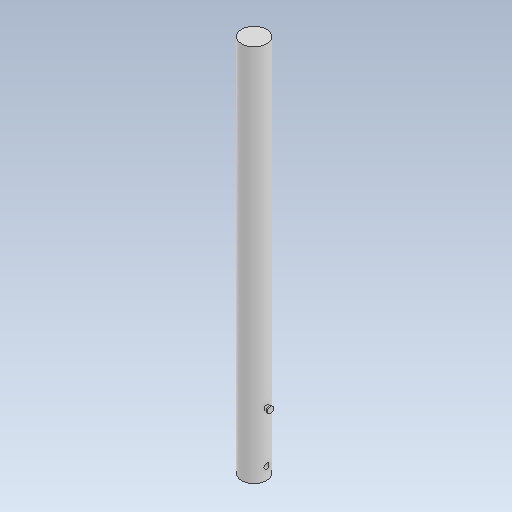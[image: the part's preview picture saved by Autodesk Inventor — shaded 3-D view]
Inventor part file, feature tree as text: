
AUTODESK INVENTOR PART (.ipt)
format: ipt  version: 2020.2 (Build 242310000, 310)  size: 112,128 bytes
history: native  units: in
note: dims shown in document units (in); Inventor stores cm internally (conversion verified against a paired STEP export)
features: extrude x4, sketch x4
ambient origin geometry x8: Origin, YZ Plane, XZ Plane, XY Plane, X Axis, Y Axis, Z Axis, Center Point
bodies: Solid1 (feature_tree)
feature tree (8):
  extrude  "Extrusion1"  Depth=11.811in TaperAngle=0.0deg
  extrude  "Extrusion2"  Depth=0.1575in
  extrude  "Extrusion3"  Depth=0.1575in
  extrude  "Extrusion4"  Depth=0.0394in
  sketch  "Sketch1"  dims[d0=0.7874in d1=11.811in d2=0.0in]
  sketch  "Sketch2"  dims[d3=0.1575in d4=0.1575in]
  sketch  "Sketch3"  dims[d5=0.8268in d6=0.0in d7=0.1575in]
  sketch  "Sketch4"  dims[d8=0.4724in d9=0.0in d10=0.1969in d11=0.0394in d12=0.0in]
